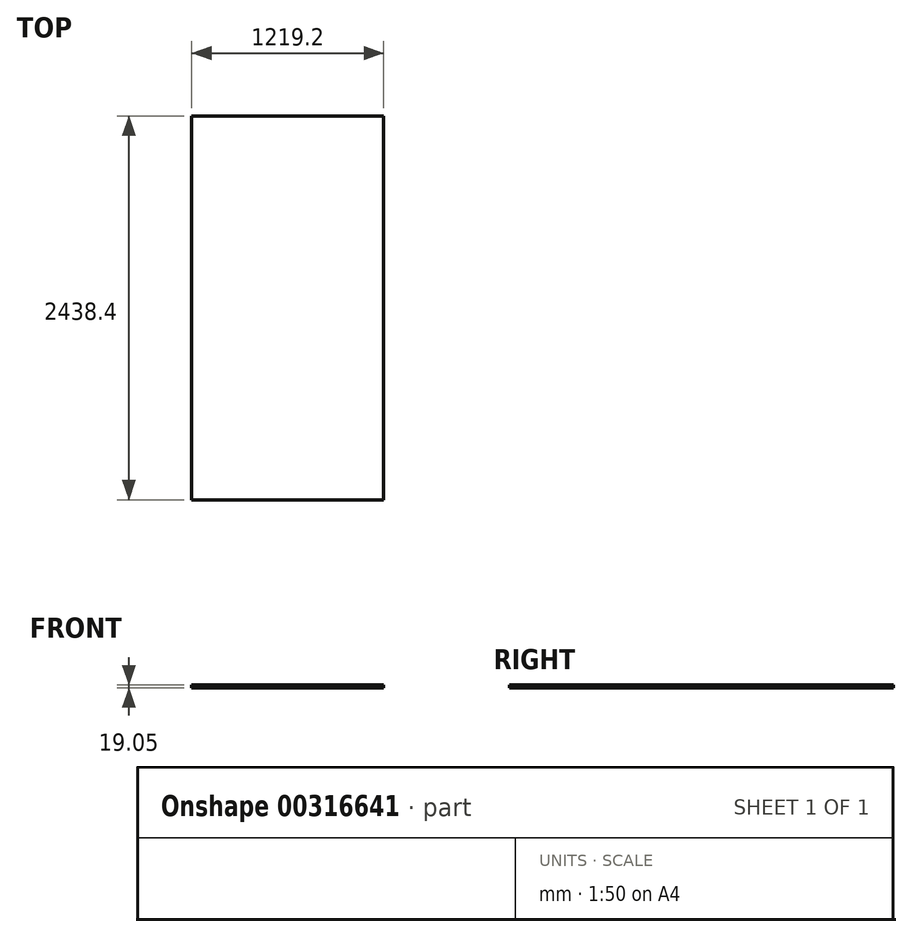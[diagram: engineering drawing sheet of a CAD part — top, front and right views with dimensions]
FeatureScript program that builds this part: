
annotation { "Feature Type Name" : "Feature", "Feature Type Description" : "" }
export const myFeature = defineFeature(function(context is Context, id is Id, definition is map)
    precondition{}
    {
        {
            var Q0;
            Q0=qCreatedBy(makeId("Front.planeOp"),FACE);
            var sketch = newSketch(context, id + "F0", { "sketchPlane" : qUnion([Q0])});
            skLineSegment(sketch, "E0.bottom", {"start": v(-63.57, 0) * mm, "end": v(1155.63, 0) * mm});
            skLineSegment(sketch, "E0.top", {"start": v(-63.57, -19.05) * mm, "end": v(1155.63, -19.05) * mm});
            skLineSegment(sketch, "E0.left", {"start": v(-63.57, 0) * mm, "end": v(-63.57, -19.05) * mm});
            skLineSegment(sketch, "E0.right", {"start": v(1155.63, 0) * mm, "end": v(1155.63, -19.05) * mm});
            skSolve(sketch);
        }
        {
            var Q0;
            Q0=makeQuery(id+"F0.imprint","IMPRINT",FACE,{"disambiguationData":[TD([[makeQuery(id+"F0.imprint","IMPRINT",EDGE,{"derivedFrom":sQuery(id+"F0.wireOp",EDGE,"E0.bottom")}),-1.0]])]});
            extrude(context, id + "F1", {"entities" : qUnion([Q0]), "depth" : 2438.4 * mm});
        }
    });
